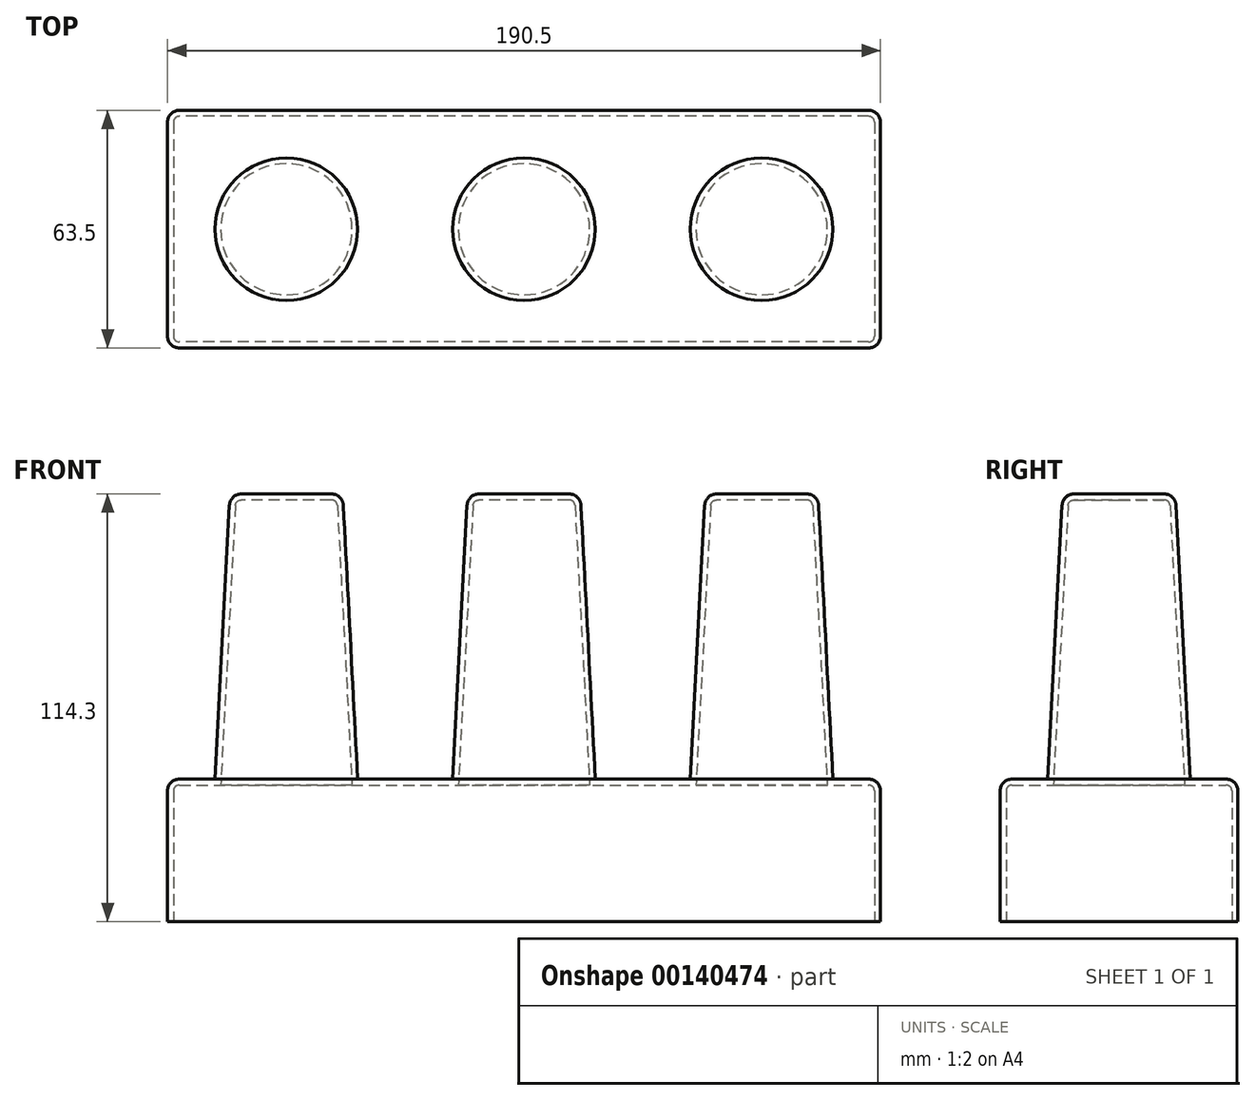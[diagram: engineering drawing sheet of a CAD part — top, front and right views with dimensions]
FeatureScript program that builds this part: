
annotation { "Feature Type Name" : "Feature", "Feature Type Description" : "" }
export const myFeature = defineFeature(function(context is Context, id is Id, definition is map)
    precondition{}
    {
        {
            var Q0;
            Q0=qCreatedBy(makeId("Top.planeOp"),FACE);
            var sketch = newSketch(context, id + "F0", { "sketchPlane" : qUnion([Q0])});
            skLineSegment(sketch, "E0.bottom", {"start": v(95.25, 31.75) * mm, "end": v(-95.25, 31.75) * mm});
            skLineSegment(sketch, "E0.top", {"start": v(95.25, -31.75) * mm, "end": v(-95.25, -31.75) * mm});
            skLineSegment(sketch, "E0.left", {"start": v(95.25, 31.75) * mm, "end": v(95.25, -31.75) * mm});
            skLineSegment(sketch, "E0.right", {"start": v(-95.25, 31.75) * mm, "end": v(-95.25, -31.75) * mm});
            skPoint(sketch, "E0.middle", {"position": v(0, 0) * mm});
            skSolve(sketch);
        }
        {
            var Q0;
            Q0=makeQuery(id+"F0.imprint","IMPRINT",FACE,{"disambiguationData":[TD([[makeQuery(id+"F0.imprint","IMPRINT",EDGE,{"derivedFrom":sQuery(id+"F0.wireOp",EDGE,"E0.bottom")}),1.0]])]});
            extrude(context, id + "F4", {"entities" : qUnion([Q0]), "depth" : 38.1 * mm});
        }
        {
            var Q0;
            Q0=makeQuery(id+"F4.opExtrude","CAP_FACE",FACE,{"disambiguationData":[OSD([sQuery(id+"F0.wireOp",EDGE,"E0.bottom"),sQuery(id+"F0.wireOp",EDGE,"E0.top"),sQuery(id+"F0.wireOp",EDGE,"E0.left"),sQuery(id+"F0.wireOp",EDGE,"E0.right")])],"isStart":false});
            var sketch = newSketch(context, id + "F1", { "sketchPlane" : qUnion([Q0])});
            skCircle(sketch, "E1", {"center": v(-63.5, 0) * mm, "radius": 19.05 * mm});
            skCircle(sketch, "E2", {"center": v(0, 0) * mm, "radius": 19.05 * mm});
            skCircle(sketch, "E3", {"center": v(63.5, 0) * mm, "radius": 19.05 * mm});
            skSolve(sketch);
        }
        {
            var Q0;
            Q0 = qSketchRegion(id + "F1", true);
            extrude(context, id + "F2", {"entities" : qUnion([Q0]), "operationType" : NewBodyOperationType.ADD, "depth" : 76.2 * mm, "hasDraft" : true, "draftAngle" : 3 * degree, "draftPullDirection" : true});
        }
        {
            var Q0;
            Q0=makeQuery(id+"F4.opExtrude","SWEPT_EDGE",EDGE,{"disambiguationData":[OSD([sQuery(id+"F0.wireOp",EDGE,"E0.top"),sQuery(id+"F0.wireOp",EDGE,"E0.left")])]});
            var Q1;
            Q1=makeQuery(id+"F4.opExtrude","CAP_EDGE",EDGE,{"disambiguationData":[OSD([sQuery(id+"F0.wireOp",EDGE,"E0.left")])],"isStart":false});
            var Q2;
            Q2=makeQuery(id+"F4.opExtrude","SWEPT_EDGE",EDGE,{"disambiguationData":[OSD([sQuery(id+"F0.wireOp",EDGE,"E0.bottom"),sQuery(id+"F0.wireOp",EDGE,"E0.left")])]});
            var Q3;
            Q3=makeQuery(id+"F4.opExtrude","CAP_EDGE",EDGE,{"disambiguationData":[OSD([sQuery(id+"F0.wireOp",EDGE,"E0.bottom")])],"isStart":false});
            var Q4;
            Q4=makeQuery(id+"F4.opExtrude","SWEPT_EDGE",EDGE,{"disambiguationData":[OSD([sQuery(id+"F0.wireOp",EDGE,"E0.bottom"),sQuery(id+"F0.wireOp",EDGE,"E0.right")])]});
            var Q5;
            Q5=makeQuery(id+"F4.opExtrude","SWEPT_EDGE",EDGE,{"disambiguationData":[OSD([sQuery(id+"F0.wireOp",EDGE,"E0.top"),sQuery(id+"F0.wireOp",EDGE,"E0.right")])]});
            var Q6;
            Q6=makeQuery(id+"F2.opExtrude","CAP_FACE",FACE,{"disambiguationData":[OSD([sQuery(id+"F1.wireOp",EDGE,"E1")])],"isStart":false});
            var Q7;
            Q7=makeQuery(id+"F2.opExtrude","CAP_FACE",FACE,{"disambiguationData":[OSD([sQuery(id+"F1.wireOp",EDGE,"E2")])],"isStart":false});
            var Q8;
            Q8=makeQuery(id+"F2.opExtrude","CAP_FACE",FACE,{"disambiguationData":[OSD([sQuery(id+"F1.wireOp",EDGE,"E3")])],"isStart":false});
            var Q9;
            Q9=makeQuery(id+"F4.opExtrude","CAP_EDGE",EDGE,{"disambiguationData":[OSD([sQuery(id+"F0.wireOp",EDGE,"E0.right")])],"isStart":false});
            var Q10;
            Q10=makeQuery(id+"F2.opExtrude","CAP_EDGE",EDGE,{"disambiguationData":[OSD([sQuery(id+"F1.wireOp",EDGE,"E3")])],"isStart":true});
            var Q11;
            Q11=makeQuery(id+"F2.opExtrude","CAP_EDGE",EDGE,{"disambiguationData":[OSD([sQuery(id+"F1.wireOp",EDGE,"E2")])],"isStart":true});
            var Q12;
            Q12=makeQuery(id+"F4.opExtrude","CAP_EDGE",EDGE,{"disambiguationData":[OSD([sQuery(id+"F0.wireOp",EDGE,"E0.top")])],"isStart":false});
            var Q13;
            Q13=makeQuery(id+"F2.opExtrude","CAP_EDGE",EDGE,{"disambiguationData":[OSD([sQuery(id+"F1.wireOp",EDGE,"E1")])],"isStart":true});
            fillet(context, id + "F3", {"entities" : qUnion([Q0, Q1, Q2, Q3, Q4, Q5, Q6, Q7, Q8, Q9, Q10, Q11, Q12, Q13]), "radius" : 3.17 * mm, "tangentPropagation" : true, "allowEdgeOverflow" : false});
        }
        {
            var Q0;
            Q0=makeQuery(id+"F4.opExtrude","CAP_FACE",FACE,{"disambiguationData":[OSD([sQuery(id+"F0.wireOp",EDGE,"E0.bottom"),sQuery(id+"F0.wireOp",EDGE,"E0.top"),sQuery(id+"F0.wireOp",EDGE,"E0.left"),sQuery(id+"F0.wireOp",EDGE,"E0.right")])],"isStart":true});
            shell(context, id + "F5", {"entities" : qUnion([Q0]), "thickness" : 1.59 * mm});
        }
    });
